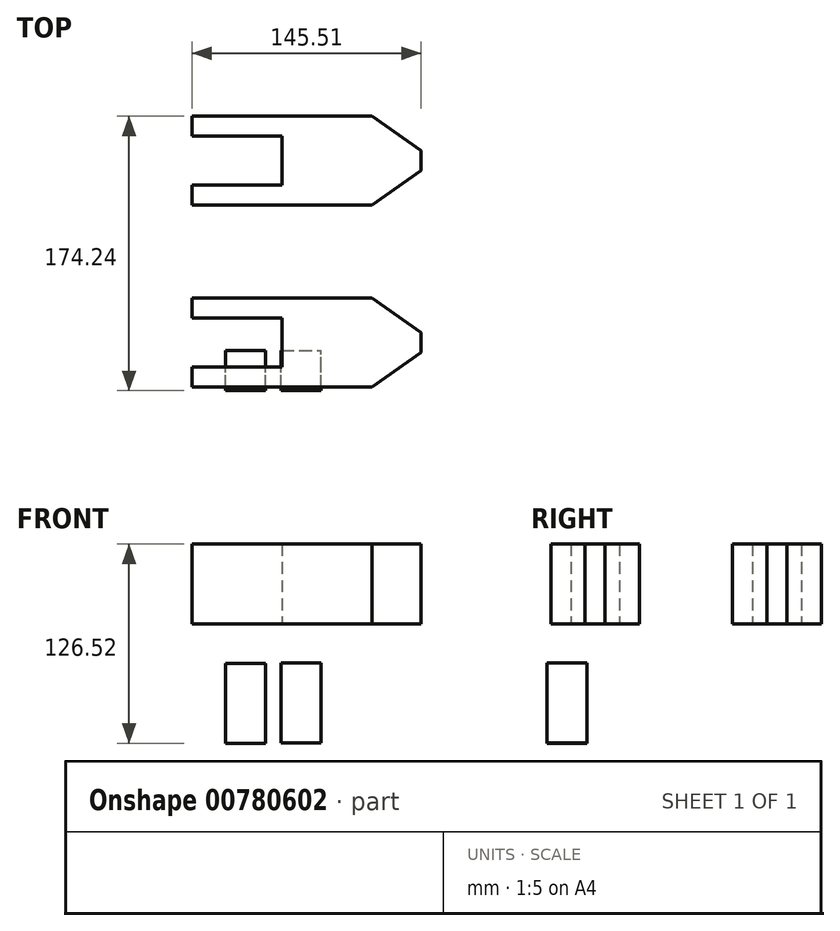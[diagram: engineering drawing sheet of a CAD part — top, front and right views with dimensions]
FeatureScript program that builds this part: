
annotation { "Feature Type Name" : "Feature", "Feature Type Description" : "" }
export const myFeature = defineFeature(function(context is Context, id is Id, definition is map)
    precondition{}
    {
        {
            var Q0;
            Q0=qCreatedBy(makeId("Front.planeOp"),FACE);
            var sketch = newSketch(context, id + "F0", { "sketchPlane" : qUnion([Q0])});
            skLineSegment(sketch, "E0.bottom", {"start": v(-48.37, -24.92) * mm, "end": v(-22.97, -24.92) * mm});
            skLineSegment(sketch, "E0.top", {"start": v(-48.37, -75.72) * mm, "end": v(-22.97, -75.72) * mm});
            skLineSegment(sketch, "E0.left", {"start": v(-48.37, -24.92) * mm, "end": v(-48.37, -75.72) * mm});
            skLineSegment(sketch, "E0.right", {"start": v(-22.97, -24.92) * mm, "end": v(-22.97, -75.72) * mm});
            skLineSegment(sketch, "E1.bottom", {"start": v(-13.3, -24.74) * mm, "end": v(12.1, -24.74) * mm});
            skLineSegment(sketch, "E1.top", {"start": v(-13.3, -75.54) * mm, "end": v(12.1, -75.54) * mm});
            skLineSegment(sketch, "E1.left", {"start": v(-13.3, -24.74) * mm, "end": v(-13.3, -75.54) * mm});
            skLineSegment(sketch, "E1.right", {"start": v(12.1, -24.74) * mm, "end": v(12.1, -75.54) * mm});
            skSolve(sketch);
        }
        {
            var Q0;
            Q0=qSketchRegion(id+"F0",true);
            extrude(context, id + "F1", {"entities" : qUnion([Q0]), "depth" : 25.4 * mm, "offsetDistance" : 25.4 * mm});
        }
        {
            var Q0;
            Q0=qCreatedBy(makeId("Top.planeOp"),FACE);
            var sketch = newSketch(context, id + "F2", { "sketchPlane" : qUnion([Q0])});
            skLineSegment(sketch, "E2", {"start": v(-69.72, 33.35) * mm, "end": v(44.58, 33.35) * mm});
            skLineSegment(sketch, "E3", {"start": v(44.58, 33.35) * mm, "end": v(75.79, 11.5) * mm});
            skLineSegment(sketch, "E4", {"start": v(75.79, 11.5) * mm, "end": v(75.79, -1.2) * mm});
            skLineSegment(sketch, "E5", {"start": v(75.79, -1.2) * mm, "end": v(44.58, -23.05) * mm});
            skLineSegment(sketch, "E6", {"start": v(-69.72, -23.05) * mm, "end": v(44.58, -23.05) * mm});
            skLineSegment(sketch, "E7", {"start": v(44.58, -23.05) * mm, "end": v(44.58, 33.35) * mm, "construction": true});
            skLineSegment(sketch, "E8", {"start": v(-69.72, -23.05) * mm, "end": v(-69.72, -10.35) * mm});
            skLineSegment(sketch, "E9", {"start": v(-69.72, 33.35) * mm, "end": v(-69.72, 20.65) * mm});
            skLineSegment(sketch, "E10", {"start": v(-69.72, 20.65) * mm, "end": v(-12.57, 20.65) * mm});
            skLineSegment(sketch, "E11", {"start": v(-69.72, -10.35) * mm, "end": v(-12.57, -10.35) * mm});
            skLineSegment(sketch, "E12", {"start": v(-12.57, -10.35) * mm, "end": v(-12.57, 20.65) * mm});
            skLineSegment(sketch, "E13", {"start": v(-99.9, 62.9) * mm, "end": v(116.58, 62.9) * mm, "construction": true});
            skLineSegment(sketch, "E14.MirrorCS", {"start": v(-69.72, 92.43) * mm, "end": v(44.58, 92.43) * mm});
            skLineSegment(sketch, "E15.MirrorCS", {"start": v(-69.72, 105.13) * mm, "end": v(-12.57, 105.13) * mm});
            skLineSegment(sketch, "E16.MirrorCS", {"start": v(-12.57, 136.14) * mm, "end": v(-12.57, 105.13) * mm});
            skLineSegment(sketch, "E17.MirrorCS", {"start": v(-69.72, 136.14) * mm, "end": v(-12.57, 136.14) * mm});
            skLineSegment(sketch, "E18.MirrorCS", {"start": v(-69.72, 148.84) * mm, "end": v(44.58, 148.84) * mm});
            skLineSegment(sketch, "E19.MirrorCS", {"start": v(75.79, 126.99) * mm, "end": v(44.58, 148.84) * mm});
            skLineSegment(sketch, "E20.MirrorCS", {"start": v(75.79, 114.29) * mm, "end": v(75.79, 126.99) * mm});
            skLineSegment(sketch, "E21.MirrorCS", {"start": v(44.58, 92.43) * mm, "end": v(75.79, 114.29) * mm});
            skLineSegment(sketch, "E22.MirrorCS", {"start": v(-69.72, 148.84) * mm, "end": v(-69.72, 136.14) * mm});
            skLineSegment(sketch, "E23.MirrorCS", {"start": v(-69.72, 92.43) * mm, "end": v(-69.72, 105.13) * mm});
            skSolve(sketch);
        }
        {
            var Q0;
            Q0=qSketchRegion(id+"F2",true);
            extrude(context, id + "F3", {"entities" : qUnion([Q0]), "depth" : 50.8 * mm, "offsetDistance" : 25.4 * mm});
        }
    });
